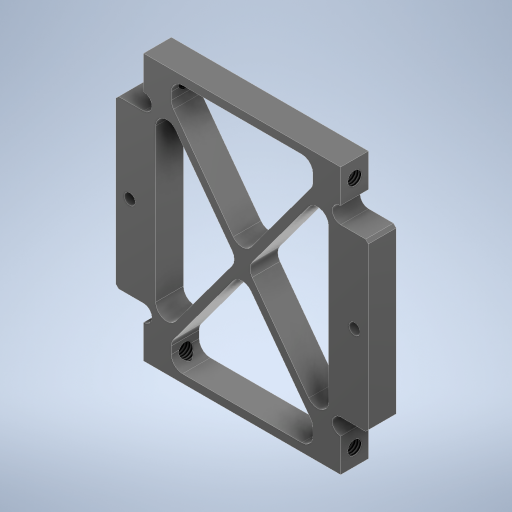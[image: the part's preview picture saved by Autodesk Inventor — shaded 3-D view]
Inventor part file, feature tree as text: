
AUTODESK INVENTOR PART (.ipt)
format: ipt  version: 2024.2 (Build 282272000, 272)  size: 382,976 bytes
history: native  units: mm
features: sketch x2, hole x2, extrude x1, chamfer x1, mirror x1
ambient origin geometry x8: Origin, YZ Plane, XZ Plane, XY Plane, X Axis, Y Axis, Z Axis, Center Point
bodies: Solid1 (feature_tree)
feature tree (7):
  sketch  "Sketch1"  dims[d0=1.5mm d1=5.0mm]
  extrude  "Extrusion1"  Depth=5.0mm
  hole  "Side-M3"  [1 undecoded]
  hole  "Phi2-H7"  [1 undecoded]
  chamfer  "C0.5"  Distance=5.0mm
  mirror  "Mirror1"
  sketch  "Sketch2"  dims[d2=48.0mm d3=9.0mm d4=35.5mm d5=5.0mm d6=1.5mm d8=1.5mm d9=1.5mm d10=5.0mm d11=0.0mm d12=2.459mm d13=6.0mm d14=4.0mm d15=2.0mm d16=90.0deg d17=5.0mm d18=0.0mm d19=0.5mm d20=2.0mm d21=45.0deg d22=2.0mm d24=2.0mm d25=2.0mm d26=6.0mm d27=4.0mm d28=2.0mm d29=90.0deg d30=8.0mm d31=0.0mm]
note: 2 required parameter values undecoded (feature->parameter linkage not recoverable at this tier; creation-order binding heuristic only, values carry confidence <= 0.55)
